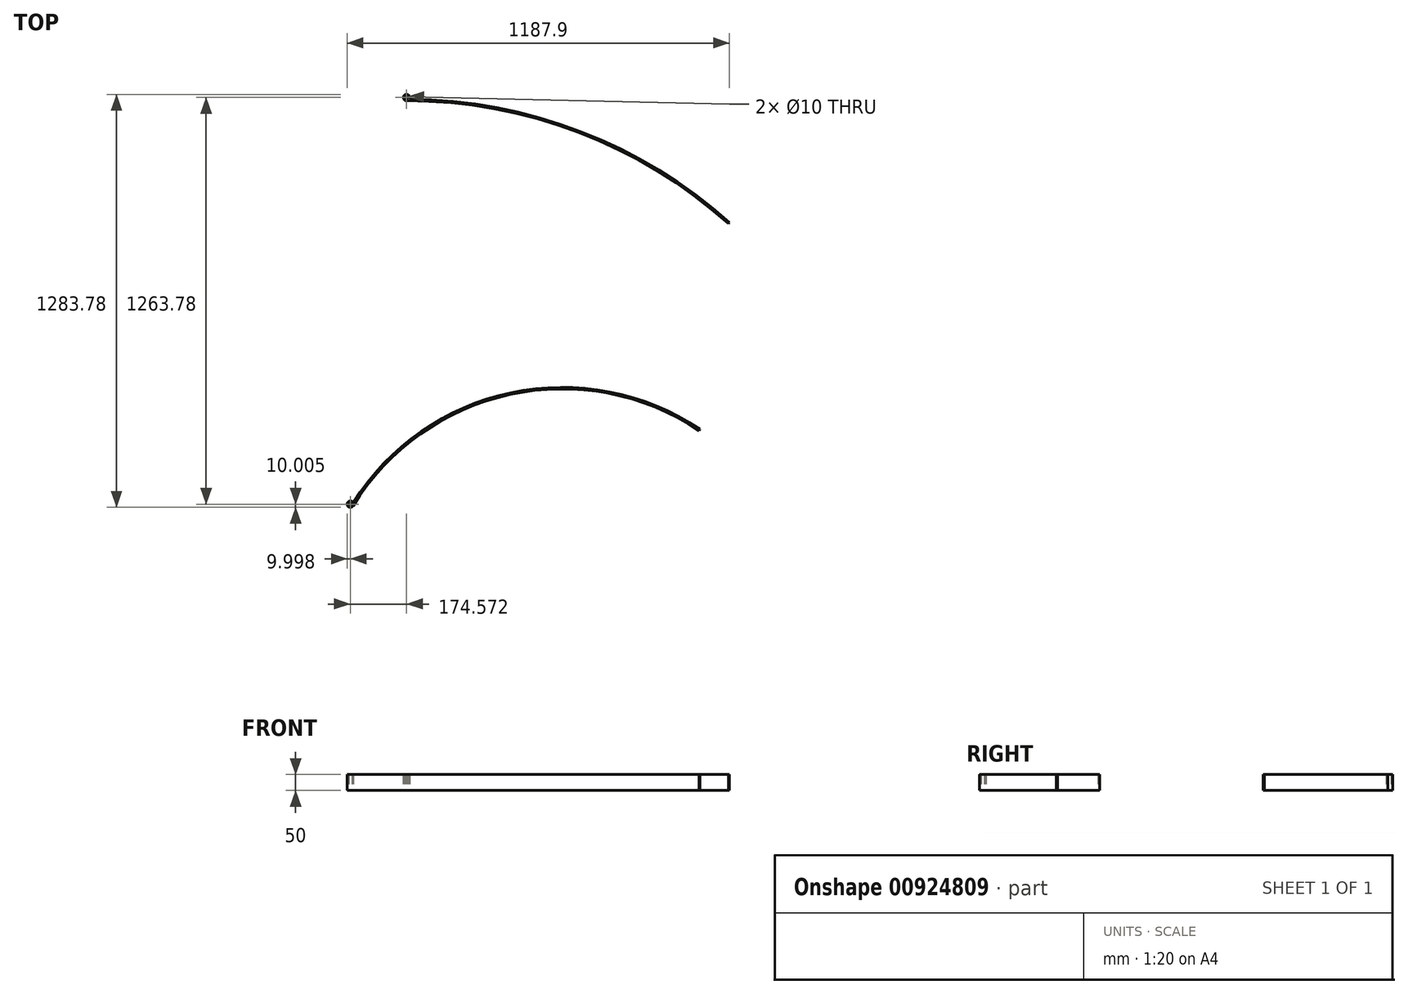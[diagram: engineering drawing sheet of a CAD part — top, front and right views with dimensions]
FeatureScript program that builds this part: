
annotation { "Feature Type Name" : "Feature", "Feature Type Description" : "" }
export const myFeature = defineFeature(function(context is Context, id is Id, definition is map)
    precondition{}
    {
        {
            var Q0;
            Q0=qCreatedBy(makeId("Top.planeOp"),FACE);
            var sketch = newSketch(context, id + "F0", { "sketchPlane" : qUnion([Q0])});
            skArc(sketch, "E0", {"start": v(1000, 1118.03) * mm, "mid": v(535.23, 1401.26) * mm, "end": v(0, 1500) * mm});
            skArc(sketch, "E1.0", {"start": v(1003.33, 1121.76) * mm, "mid": v(537.02, 1405.93) * mm, "end": v(0, 1505) * mm});
            skCircle(sketch, "E2", {"center": v(0, 1510) * mm, "radius": 10 * mm});
            skCircle(sketch, "E3.0", {"center": v(0, 1510) * mm, "radius": 5 * mm});
            skLineSegment(sketch, "E4", {"start": v(0, 1505) * mm, "end": v(0, 1500) * mm});
            skLineSegment(sketch, "E5", {"start": v(1000, 1118.03) * mm, "end": v(1003.33, 1121.76) * mm});
            skArc(sketch, "E6", {"start": v(1015.92, 226.94) * mm, "mid": v(366.27, 590.3) * mm, "end": v(-283.37, 226.94) * mm});
            skArc(sketch, "E7", {"start": v(-223.73, 190.3) * mm, "mid": v(366.27, 520.3) * mm, "end": v(956.27, 190.3) * mm});
            skLineSegment(sketch, "E8", {"start": v(956.27, 190.3) * mm, "end": v(1015.92, 226.94) * mm});
            skLineSegment(sketch, "E9", {"start": v(-223.73, 190.3) * mm, "end": v(-283.37, 226.94) * mm});
            skLineSegment(sketch, "E10", {"start": v(366.27, 190.3) * mm, "end": v(956.27, 190.3) * mm});
            skLineSegment(sketch, "E11", {"start": v(366.27, 190.3) * mm, "end": v(366.27, 520.3) * mm});
            skLineSegment(sketch, "E12", {"start": v(366.27, 190.3) * mm, "end": v(-223.73, 190.3) * mm});
            skArc(sketch, "E13.0", {"start": v(1020.18, 229.56) * mm, "mid": v(366.27, 595.3) * mm, "end": v(-287.63, 229.56) * mm});
            skSolve(sketch);
        }
        {
            var Q0;
            {var subQ0=sQuery(id+"F0.wireOp",EDGE,"E4");var subQ1=sQuery(id+"F0.wireOp",EDGE,"E1.0");var subQ2=makeQuery(id+"F0.imprint","INTERSECT",VERTEX,{"derivedFrom":[subQ1,subQ0]});Q0=makeQuery(id+"F0.imprint","IMPRINT",FACE,{"disambiguationData":[TD([[makeQuery(id+"F0.imprint","IMPRINT",EDGE,{"disambiguationData":[TD([[subQ2,1.0]])],"derivedFrom":subQ1}),1.0]])]});}
            var Q1;
            Q1=makeQuery(id+"F0.imprint","IMPRINT",FACE,{"disambiguationData":[TD([[makeQuery(id+"F0.imprint","IMPRINT",EDGE,{"derivedFrom":sQuery(id+"F0.wireOp",EDGE,"E3.0")}),-1.0]])]});
            var Q2;
            {var subQ1=sQuery(id+"F0.wireOp",EDGE,"E0");Q2=makeQuery(id+"F0.imprint","IMPRINT",FACE,{"disambiguationData":[TD([[makeQuery(id+"F0.imprint","IMPRINT",EDGE,{"derivedFrom":subQ1}),-1.0]])]});}
            extrude(context, id + "F1", {"entities" : qUnion([Q0, Q1, Q2]), "depth" : 50 * mm, "offsetDistance" : 25 * mm});
        }
        {
            var Q0;
            Q0=qCreatedBy(makeId("Top.planeOp"),FACE);
            var sketch = newSketch(context, id + "F2", { "sketchPlane" : qUnion([Q0])});
            skArc(sketch, "E14", {"start": v(1133.24, 241) * mm, "mid": v(483.6, 604.36) * mm, "end": v(-166.05, 241) * mm});
            skArc(sketch, "E15", {"start": v(-106.4, 204.36) * mm, "mid": v(483.6, 534.36) * mm, "end": v(1073.6, 204.36) * mm});
            skLineSegment(sketch, "E16", {"start": v(1073.6, 204.36) * mm, "end": v(1133.24, 241) * mm});
            skLineSegment(sketch, "E17", {"start": v(-106.4, 204.36) * mm, "end": v(-166.05, 241) * mm});
            skLineSegment(sketch, "E18", {"start": v(483.6, 204.36) * mm, "end": v(1073.6, 204.36) * mm});
            skLineSegment(sketch, "E19", {"start": v(483.6, 204.36) * mm, "end": v(483.6, 534.36) * mm});
            skLineSegment(sketch, "E20", {"start": v(483.6, 204.36) * mm, "end": v(-106.4, 204.36) * mm});
            skArc(sketch, "E21.0", {"start": v(1137.5, 243.62) * mm, "mid": v(483.6, 609.36) * mm, "end": v(-170.31, 243.62) * mm});
            skCircle(sketch, "E22", {"center": v(-174.57, 246.23) * mm, "radius": 10 * mm});
            skCircle(sketch, "E23.0", {"center": v(-174.57, 246.23) * mm, "radius": 5 * mm});
            skLineSegment(sketch, "E24", {"start": v(-166.05, 241) * mm, "end": v(-170.31, 243.62) * mm});
            skLineSegment(sketch, "E25", {"start": v(-174.57, 246.23) * mm, "end": v(-170.31, 243.62) * mm});
            skLineSegment(sketch, "E26", {"start": v(908.82, 474.77) * mm, "end": v(911.61, 478.92) * mm});
            skSolve(sketch);
        }
        {
            var Q0;
            {var subQ1=sQuery(id+"F2.wireOp",EDGE,"E23.0");Q0=makeQuery(id+"F2.imprint","IMPRINT",FACE,{"disambiguationData":[TD([[makeQuery(id+"F2.imprint","IMPRINT",EDGE,{"derivedFrom":subQ1}),-1.0]])]});}
            var Q1;
            {var subQ0=sQuery(id+"F2.wireOp",EDGE,"E24");Q1=makeQuery(id+"F2.imprint","IMPRINT",FACE,{"disambiguationData":[TD([[makeQuery(id+"F2.imprint","IMPRINT",EDGE,{"derivedFrom":subQ0}),-1.0]])]});}
            var Q2;
            {var subQ3=sQuery(id+"F2.wireOp",EDGE,"E26");Q2=makeQuery(id+"F2.imprint","IMPRINT",FACE,{"disambiguationData":[TD([[makeQuery(id+"F2.imprint","IMPRINT",EDGE,{"derivedFrom":subQ3}),1.0]])]});}
            extrude(context, id + "F3", {"entities" : qUnion([Q0, Q1, Q2]), "depth" : 50 * mm, "offsetDistance" : 25 * mm});
        }
    });
